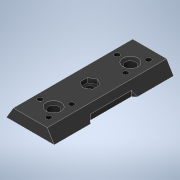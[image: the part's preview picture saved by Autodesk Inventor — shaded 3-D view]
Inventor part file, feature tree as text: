
AUTODESK INVENTOR PART (.ipt)
format: ipt  version: 2021 (Build 250183000, 183)  size: 209,408 bytes
history: native  units: mm
features: extrude x5, sketch x5, chamfer x1, projected_geometry x1
ambient origin geometry x8: Origin, YZ Plane, XZ Plane, XY Plane, X Axis, Y Axis, Z Axis, Center Point
bodies: Solid2 (feature_tree)
feature tree (12):
  extrude  "Extrusion5"  Depth=10.0mm
  extrude  "Extrusion6"  Depth=5.0mm
  extrude  "Extrusion7"  Depth=2.2mm
  extrude  "Extrusion8"  Depth=14.8mm
  chamfer  "Chamfer2"  Distance=5.0mm
  extrude  "Extrusion9"  Depth=52.0mm TaperAngle=0.0deg
  sketch  "Sketch1"  dims[d0=10.0mm d1=10.0mm]
  sketch  "Sketch5"  dims[d2=10.0mm d3=5.0mm]
  sketch  "Sketch6"  dims[d4=5.774mm d11=2.2mm]
  projected_geometry  "Projected Loop4"
  sketch  "Sketch7"  dims[d12=4.5mm d38=14.8mm]
  sketch  "Sketch8"  dims[d39=20.8mm d40=5.0mm d41=52.0mm d42=0.0mm d43=10.0mm d44=10.0mm d45=10.0mm d46=5.0mm d47=5.774mm d48=2.2mm d49=4.5mm d51=33.5mm d52=0.0mm d53=0.0mm d54=4.5mm d55=2.0mm d56=0.0mm d57=1.0mm d58=2.0mm d59=45.0deg d60=3.2mm d62=2.0mm d63=0.0mm d64=5.6mm d65=3.639746mm d66=2.5mm d67=16.75mm d68=9.0mm d70=4.0mm d71=18.0mm d72=25.0mm d73=0.0mm d74=0.0mm]
